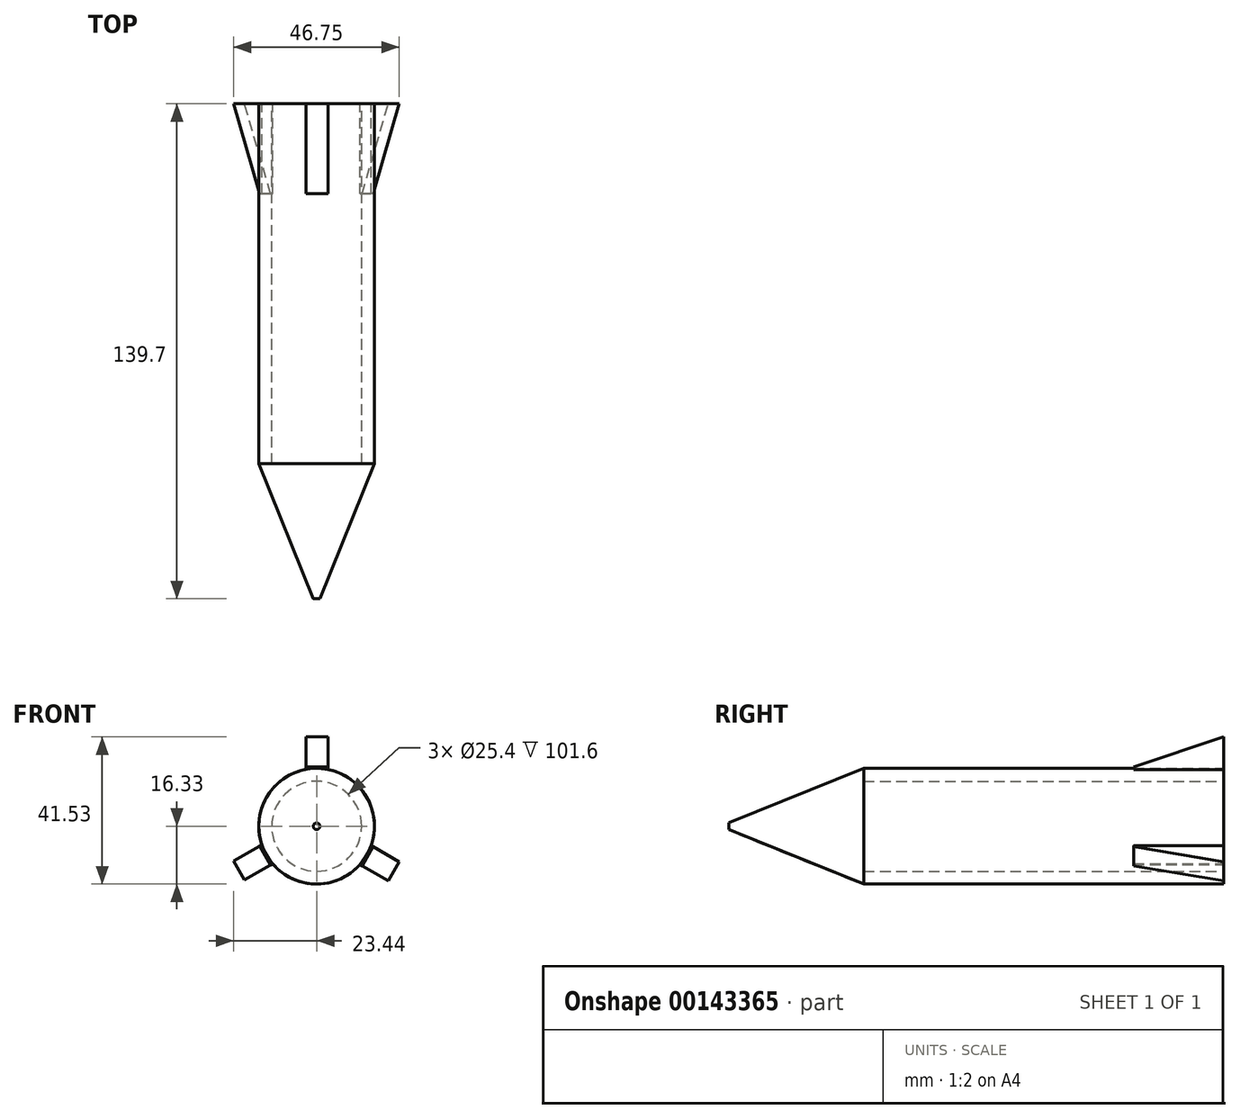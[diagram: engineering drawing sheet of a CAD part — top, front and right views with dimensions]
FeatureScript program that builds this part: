
annotation { "Feature Type Name" : "Feature", "Feature Type Description" : "" }
export const myFeature = defineFeature(function(context is Context, id is Id, definition is map)
    precondition{}
    {
        {
            var Q0;
            Q0=qCreatedBy(makeId("Front.planeOp"),FACE);
            var sketch = newSketch(context, id + "F0", { "sketchPlane" : qUnion([Q0])});
            skCircle(sketch, "E0", {"center": v(0, 0) * mm, "radius": 12.7 * mm});
            skCircle(sketch, "E1", {"center": v(0, 0) * mm, "radius": 16.33 * mm});
            skSolve(sketch);
        }
        {
            var Q0;
            Q0 = qSketchRegion(id + "F0", true);
            extrude(context, id + "F1", {"entities" : qUnion([Q0]), "depth" : 101.6 * mm});
        }
        {
            var Q0;
            Q0=makeQuery(id+"F1.opExtrude","CAP_FACE",FACE,{"disambiguationData":[OSD([sQuery(id+"F0.wireOp",EDGE,"E0"),sQuery(id+"F0.wireOp",EDGE,"E1")])],"isStart":false});
            var sketch = newSketch(context, id + "F2", { "sketchPlane" : qUnion([Q0])});
            skCircle(sketch, "E2.0", {"center": v(0, 0) * mm, "radius": 16.33 * mm});
            skSolve(sketch);
        }
        {
            var Q0;
            Q0 = qSketchRegion(id + "F2", true);
            extrude(context, id + "F3", {"entities" : qUnion([Q0]), "operationType" : NewBodyOperationType.ADD, "depth" : 38.1 * mm, "hasDraft" : true, "draftAngle" : 22 * degree, "draftPullDirection" : true});
        }
        {
            var Q0;
            Q0=qCreatedBy(makeId("Front.planeOp"),FACE);
            var sketch = newSketch(context, id + "F4", { "sketchPlane" : qUnion([Q0])});
            skLineSegment(sketch, "E3.bottom", {"start": v(3.24, 25.23) * mm, "end": v(-2.97, 25.23) * mm});
            skLineSegment(sketch, "E3.top", {"start": v(3.24, 13.63) * mm, "end": v(-2.97, 13.63) * mm});
            skLineSegment(sketch, "E3.left", {"start": v(3.24, 25.23) * mm, "end": v(3.24, 13.63) * mm});
            skLineSegment(sketch, "E3.right", {"start": v(-2.97, 25.23) * mm, "end": v(-2.97, 13.63) * mm});
            skSolve(sketch);
        }
        {
            var Q0;
            Q0 = qSketchRegion(id + "F4", true);
            extrude(context, id + "F5", {"entities" : qUnion([Q0]), "operationType" : NewBodyOperationType.ADD, "depth" : 25.4 * mm});
        }
        {
            var Q0;
            Q0=qCreatedBy(makeId("Right.planeOp"),FACE);
            var sketch = newSketch(context, id + "F6", { "sketchPlane" : qUnion([Q0])});
            skLineSegment(sketch, "E4", {"start": v(-25.54, 34.4) * mm, "end": v(-25.81, 16.6) * mm});
            skLineSegment(sketch, "E5", {"start": v(-25.81, 16.6) * mm, "end": v(26, 33.87) * mm});
            skLineSegment(sketch, "E6", {"start": v(26, 33.87) * mm, "end": v(-25.54, 34.4) * mm});
            skSolve(sketch);
        }
        {
            var Q0;
            Q0 = qSketchRegion(id + "F6", true);
            extrude(context, id + "F7", {"entities" : qUnion([Q0]), "operationType" : NewBodyOperationType.REMOVE, "endBound" : BoundingType.SYMMETRIC, "oppositeDirection" : true, "depth" : 25.4 * mm});
        }
        {
            var Q0;
            Q0=makeQuery(id+"F1.opExtrude","SWEPT_BODY",BODY,{"disambiguationData":[OSD([sQuery(id+"F0.wireOp",EDGE,"E0"),sQuery(id+"F0.wireOp",EDGE,"E1")])]});
            var Q1;
            Q1=makeQuery(id+"F1.opExtrude","CAP_EDGE",EDGE,{"disambiguationData":[OSD([sQuery(id+"F0.wireOp",EDGE,"E0")])],"isStart":true});
            circularPattern(context, id + "F8", {"entities" : qUnion([Q0]), "axis" : qUnion([Q1]), "angle" : 120 * degree, "instanceCount" : 3});
        }
    });
